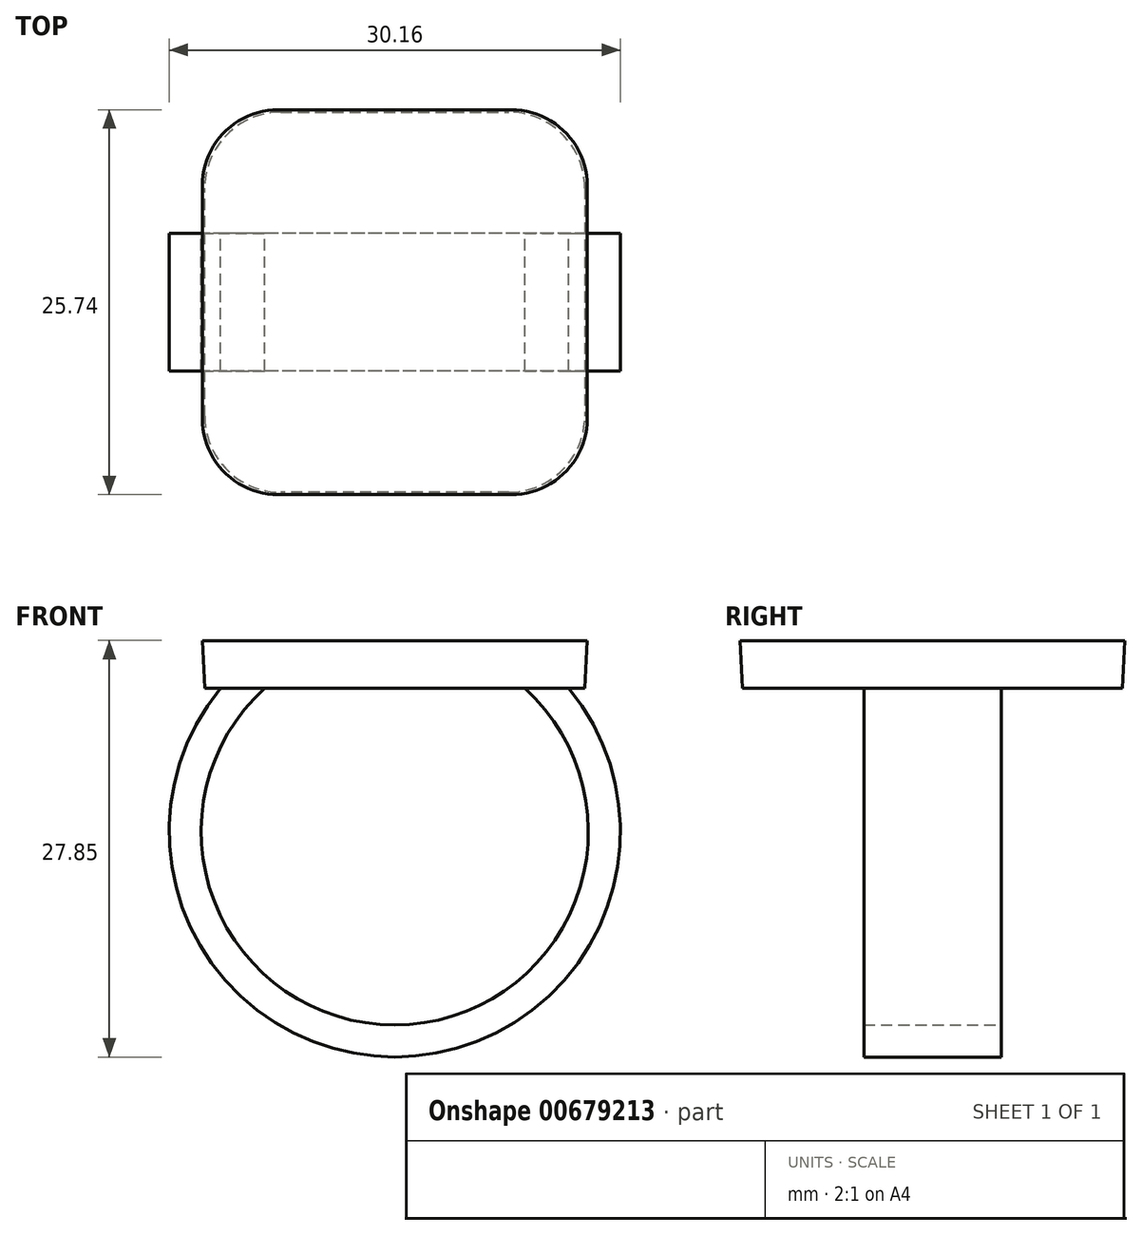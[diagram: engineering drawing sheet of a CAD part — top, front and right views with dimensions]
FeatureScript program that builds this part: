
annotation { "Feature Type Name" : "Feature", "Feature Type Description" : "" }
export const myFeature = defineFeature(function(context is Context, id is Id, definition is map)
    precondition{}
    {
        {
            var Q0;
            Q0=qCreatedBy(makeId("Top.planeOp"),FACE);
            var sketch = newSketch(context, id + "F0", { "sketchPlane" : qUnion([Q0])});
            skLineSegment(sketch, "E0.bottom", {"start": v(12.7, -12.7) * mm, "end": v(-12.7, -12.7) * mm});
            skLineSegment(sketch, "E0.top", {"start": v(12.7, 12.7) * mm, "end": v(-12.7, 12.7) * mm});
            skLineSegment(sketch, "E0.left", {"start": v(12.7, -12.7) * mm, "end": v(12.7, 12.7) * mm});
            skLineSegment(sketch, "E0.right", {"start": v(-12.7, -12.7) * mm, "end": v(-12.7, 12.7) * mm});
            skPoint(sketch, "E0.middle", {"position": v(0, 0) * mm});
            skSolve(sketch);
        }
        {
            var Q0;
            Q0=makeQuery(id+"F0.imprint","IMPRINT",FACE,{"disambiguationData":[TD([[makeQuery(id+"F0.imprint","IMPRINT",EDGE,{"derivedFrom":sQuery(id+"F0.wireOp",EDGE,"E0.bottom")}),-1.0]])]});
            extrude(context, id + "F1", {"entities" : qUnion([Q0]), "depth" : 3.17 * mm, "offsetDistance" : 25.4 * mm, "hasDraft" : true, "draftAngle" : 3 * degree});
        }
        {
            var Q0;
            Q0=qCreatedBy(makeId("Front.planeOp"),FACE);
            var sketch = newSketch(context, id + "F2", { "sketchPlane" : qUnion([Q0])});
            skArc(sketch, "E1", {"start": v(-10.16, 0) * mm, "mid": v(0, -23.56) * mm, "end": v(10.16, 0) * mm});
            skSolve(sketch);
        }
        {
            var Q0;
            Q0=makeQuery(id+"F0.imprint","IMPRINT",FACE,{"disambiguationData":[TD([[makeQuery(id+"F0.imprint","IMPRINT",EDGE,{"derivedFrom":sQuery(id+"F0.wireOp",EDGE,"E0.bottom")}),-1.0]])]});
            var sketch = newSketch(context, id + "F3", { "sketchPlane" : qUnion([Q0])});
            skLineSegment(sketch, "E2.bottom", {"start": v(11.64, -4.6) * mm, "end": v(8.69, -4.6) * mm});
            skLineSegment(sketch, "E2.top", {"start": v(11.64, 4.6) * mm, "end": v(8.69, 4.6) * mm});
            skLineSegment(sketch, "E2.left", {"start": v(11.64, -4.6) * mm, "end": v(11.64, 4.6) * mm});
            skLineSegment(sketch, "E2.right", {"start": v(8.69, -4.6) * mm, "end": v(8.69, 4.6) * mm});
            skPoint(sketch, "E2.middle", {"position": v(10.16, 0) * mm});
            skSolve(sketch);
        }
        {
            var Q0;
            Q0=makeQuery(id+"F3.imprint","IMPRINT",FACE,{"disambiguationData":[TD([[makeQuery(id+"F3.imprint","IMPRINT",EDGE,{"derivedFrom":sQuery(id+"F3.wireOp",EDGE,"E2.bottom")}),-1.0]])]});
            var Q1;
            Q1=sQuery(id+"F2.wireOp",EDGE,"E1");
            sweep(context, id + "F4", {"operationType" : NewBodyOperationType.ADD, "profiles" : qUnion([Q0]), "path" : qUnion([Q1])});
        }
        {
            var Q0;
            Q0=qCreatedBy(makeId("Front.planeOp"),FACE);
            var sketch = newSketch(context, id + "F5", { "sketchPlane" : qUnion([Q0])});
            skLineSegment(sketch, "E3.0", {"start": v(-10.07, -1.47) * mm, "end": v(-10.16, 0) * mm});
            skArc(sketch, "E3.1", {"start": v(8.69, 0) * mm, "mid": v(0, -22.53) * mm, "end": v(-8.69, 0) * mm});
            skLineSegment(sketch, "E3.2", {"start": v(12.7, 0) * mm, "end": v(-12.7, 0) * mm});
            skSolve(sketch);
        }
        {
            var Q0;
            {var subQ0=sQuery(id+"F5.wireOp",EDGE,"E3.0");Q0=makeQuery(id+"F5.imprint","IMPRINT",FACE,{"disambiguationData":[TD([[makeQuery(id+"F5.imprint","IMPRINT",EDGE,{"derivedFrom":subQ0}),-1.0]])]});}
            var Q1;
            Q1=makeQuery(id+"F4.opSweep","SWEPT_FACE",FACE,{"disambiguationData":[OSD([sQuery(id+"F2.wireOp",EDGE,"E1"),sQuery(id+"F3.wireOp",EDGE,"E2.bottom")])]});
            var Q2;
            Q2=makeQuery(id+"F4.opSweep","SWEPT_FACE",FACE,{"disambiguationData":[OSD([sQuery(id+"F2.wireOp",EDGE,"E1"),sQuery(id+"F3.wireOp",EDGE,"E2.top")])]});
            extrude(context, id + "F6", {"entities" : qUnion([Q0]), "operationType" : NewBodyOperationType.ADD, "endBound" : BoundingType.UP_TO_SURFACE, "depth" : 4.6 * mm, "endBoundEntityFace" : qUnion([Q1]), "offsetDistance" : 25.4 * mm, "hasSecondDirection" : true, "secondDirectionBound" : SecondDirectionBoundingType.UP_TO_SURFACE, "secondDirectionOppositeDirection" : true, "secondDirectionDepth" : 4.6 * mm, "secondDirectionBoundEntityFace" : qUnion([Q2])});
        }
        {
            var Q0;
            Q0=makeQuery(id+"F1.opExtrude","SWEPT_EDGE",EDGE,{"disambiguationData":[OSD([sQuery(id+"F0.wireOp",EDGE,"E0.top"),sQuery(id+"F0.wireOp",EDGE,"E0.right")])]});
            var Q1;
            Q1=makeQuery(id+"F1.opExtrude","SWEPT_EDGE",EDGE,{"disambiguationData":[OSD([sQuery(id+"F0.wireOp",EDGE,"E0.bottom"),sQuery(id+"F0.wireOp",EDGE,"E0.right")])]});
            var Q2;
            Q2=makeQuery(id+"F1.opExtrude","SWEPT_EDGE",EDGE,{"disambiguationData":[OSD([sQuery(id+"F0.wireOp",EDGE,"E0.bottom"),sQuery(id+"F0.wireOp",EDGE,"E0.left")])]});
            var Q3;
            Q3=makeQuery(id+"F1.opExtrude","SWEPT_EDGE",EDGE,{"disambiguationData":[OSD([sQuery(id+"F0.wireOp",EDGE,"E0.top"),sQuery(id+"F0.wireOp",EDGE,"E0.left")])]});
            fillet(context, id + "F7", {"entities" : qUnion([Q0, Q1, Q2, Q3]), "radius" : 5.08 * mm, "tangentPropagation" : true, "allowEdgeOverflow" : false});
        }
    });
